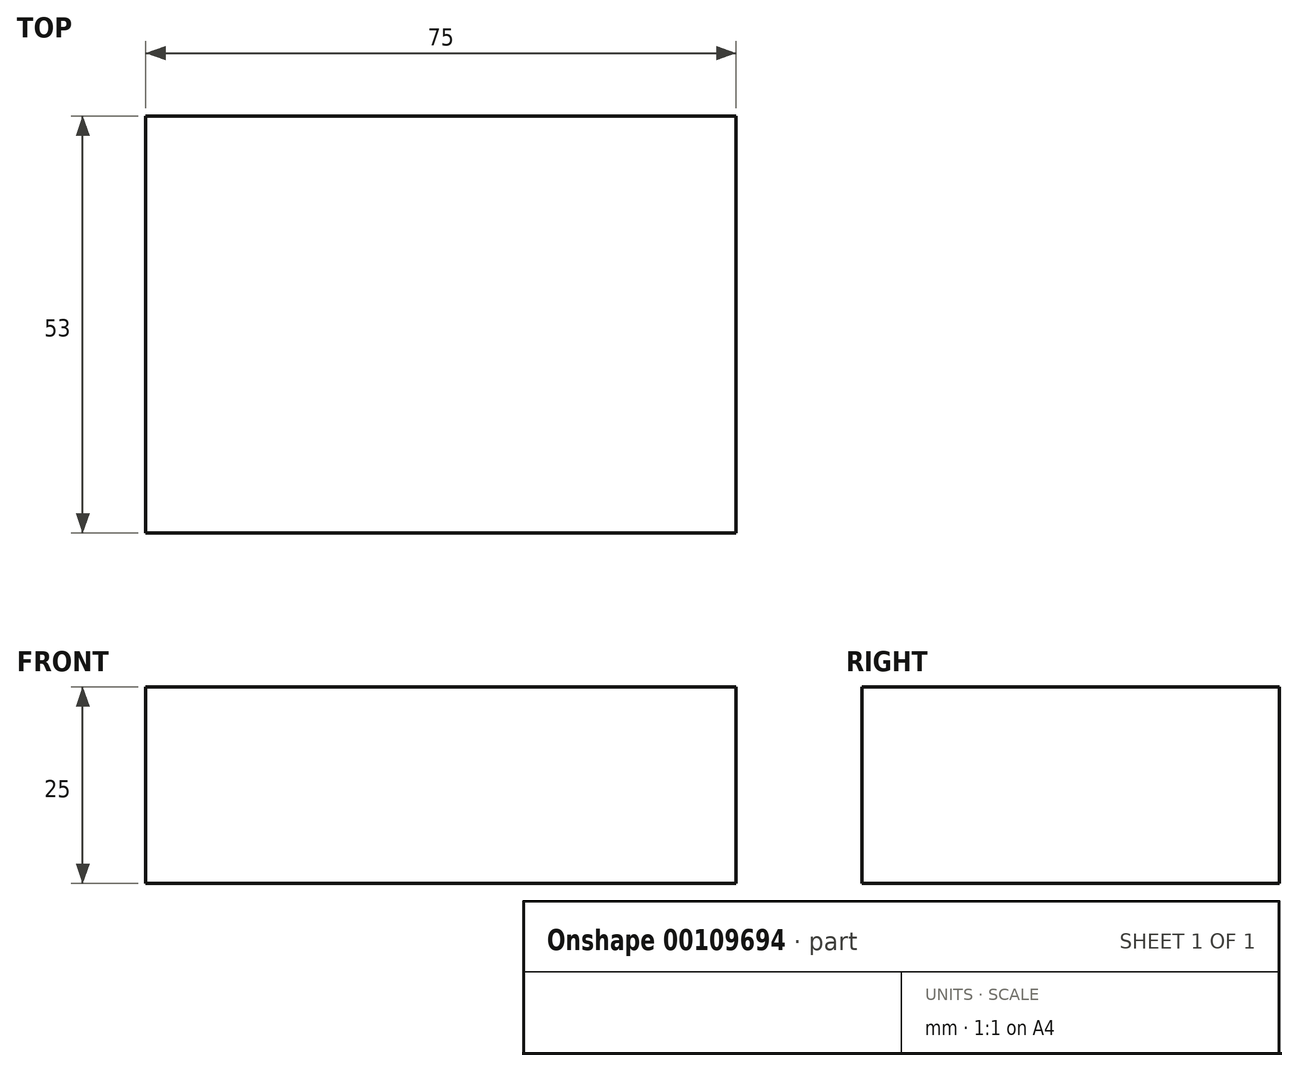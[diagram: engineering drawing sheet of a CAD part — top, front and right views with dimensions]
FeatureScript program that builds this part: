
annotation { "Feature Type Name" : "Feature", "Feature Type Description" : "" }
export const myFeature = defineFeature(function(context is Context, id is Id, definition is map)
    precondition{}
    {
        {
            var Q0;
            Q0=qCreatedBy(makeId("Top.planeOp"),FACE);
            var sketch = newSketch(context, id + "F0", { "sketchPlane" : qUnion([Q0])});
            skLineSegment(sketch, "E0", {"start": v(0, 0) * mm, "end": v(75, 0) * mm});
            skLineSegment(sketch, "E1", {"start": v(0, 0) * mm, "end": v(0, 53) * mm});
            skLineSegment(sketch, "E2", {"start": v(0, 53) * mm, "end": v(75, 53) * mm});
            skLineSegment(sketch, "E3", {"start": v(75, 0) * mm, "end": v(75, 53) * mm});
            skSolve(sketch);
        }
        {
            var Q0;
            Q0 = qSketchRegion(id + "F0", true);
            extrude(context, id + "F1", {"entities" : qUnion([Q0]), "depth" : 25 * mm});
        }
    });
